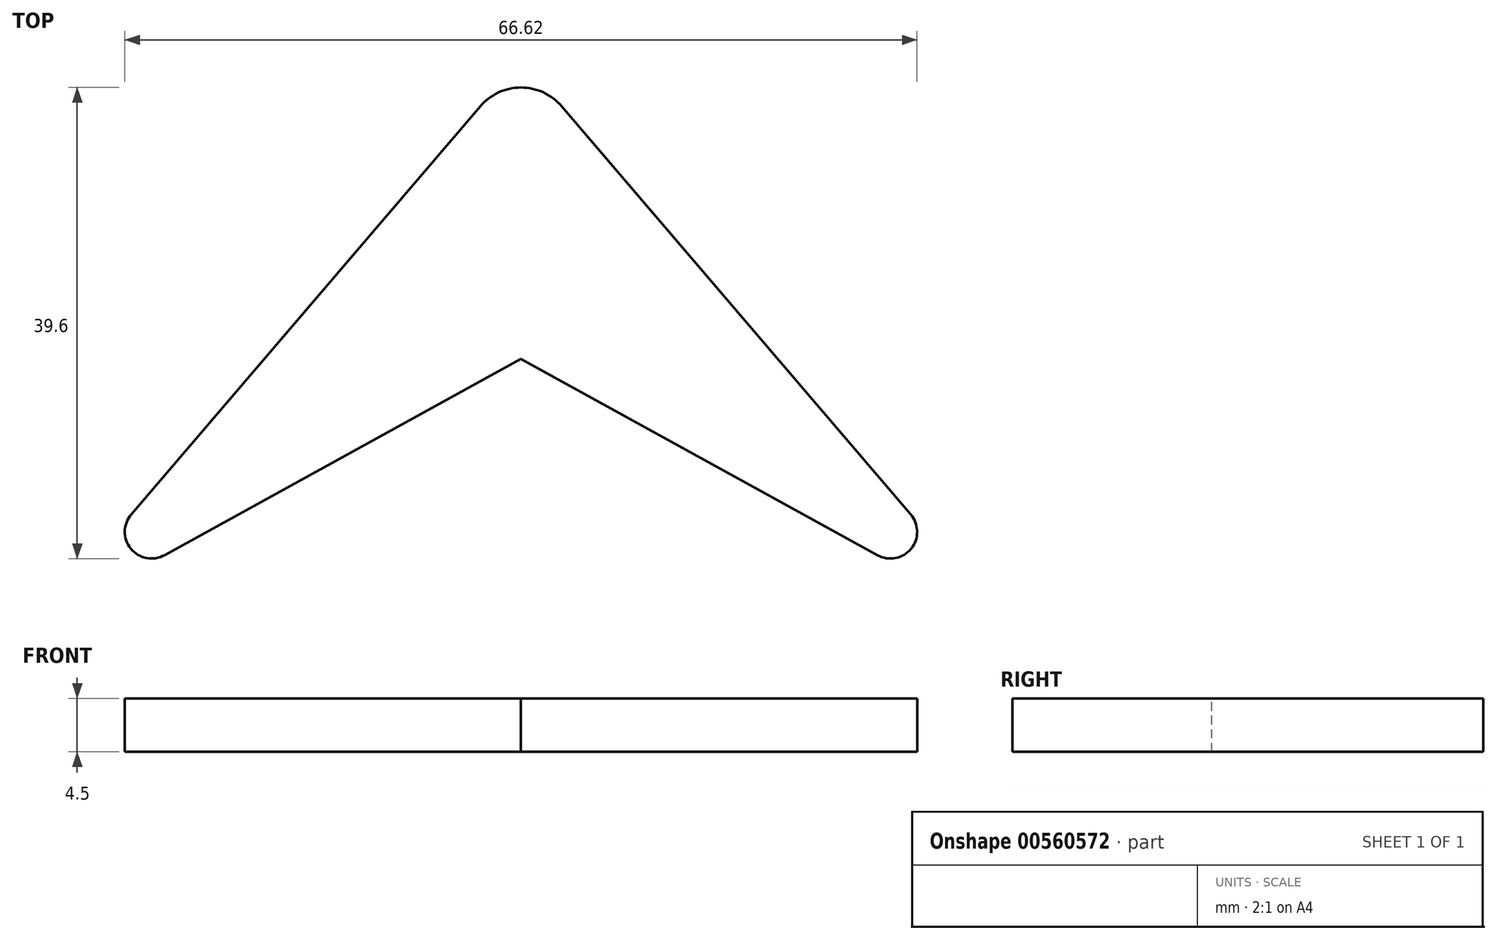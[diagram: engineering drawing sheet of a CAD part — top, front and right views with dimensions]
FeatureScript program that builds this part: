
annotation { "Feature Type Name" : "Feature", "Feature Type Description" : "" }
export const myFeature = defineFeature(function(context is Context, id is Id, definition is map)
    precondition{}
    {
        {
            var Q0;
            Q0=qCreatedBy(makeId("Top.planeOp"),FACE);
            var sketch = newSketch(context, id + "F0", { "sketchPlane" : qUnion([Q0])});
            skLineSegment(sketch, "E0", {"start": v(-21.85, -8.7) * mm, "end": v(-2.28, 14.17) * mm});
            skLineSegment(sketch, "E1", {"start": v(2.28, 14.17) * mm, "end": v(21.85, -8.7) * mm});
            skLineSegment(sketch, "E2", {"start": v(-19.99, -11) * mm, "end": v(0, 0) * mm});
            skLineSegment(sketch, "E3", {"start": v(0, 0) * mm, "end": v(19.99, -11) * mm});
            skPoint(sketch, "E4.visualSharp", {"position": v(0, 16.83) * mm});
            skArc(sketch, "E4.filletArc", {"start": v(2.28, 14.17) * mm, "mid": v(0, 15.22) * mm, "end": v(-2.28, 14.17) * mm});
            skPoint(sketch, "E5.visualSharp", {"position": v(-27.2, -14.96) * mm});
            skArc(sketch, "E5.filletArc", {"start": v(-21.85, -8.7) * mm, "mid": v(-21.87, -10.63) * mm, "end": v(-19.99, -11) * mm});
            skPoint(sketch, "E6.visualSharp", {"position": v(27.2, -14.96) * mm});
            skArc(sketch, "E6.filletArc", {"start": v(19.99, -11) * mm, "mid": v(21.87, -10.63) * mm, "end": v(21.85, -8.7) * mm});
            skSolve(sketch);
        }
        {
            var Q0;
            Q0 = qSketchRegion(id + "F0", true);
            extrude(context, id + "F1", {"entities" : qUnion([Q0]), "oppositeDirection" : true, "depth" : 3 * mm, "offsetDistance" : 25 * mm});
        }
        {
            var Q0;
            Q0=makeQuery(id+"F1.opExtrude","SWEPT_BODY",BODY,{"disambiguationData":[OSD([sQuery(id+"F0.wireOp",EDGE,"E0"),sQuery(id+"F0.wireOp",EDGE,"E1"),sQuery(id+"F0.wireOp",EDGE,"E2"),sQuery(id+"F0.wireOp",EDGE,"E3"),sQuery(id+"F0.wireOp",EDGE,"E4.filletArc"),sQuery(id+"F0.wireOp",EDGE,"E5.filletArc"),sQuery(id+"F0.wireOp",EDGE,"E6.filletArc")])]});
            var Q1;
            Q1=qCreatedBy(makeId("Origin.pointOp"),VERTEX);
            transform(context, id + "F2", {"entities" : qUnion([Q0]), "transformType" : TransformType.SCALE_UNIFORMLY, "scale" : 1.5, "scalePoint" : qUnion([Q1]), "makeCopy" : false});
        }
    });
